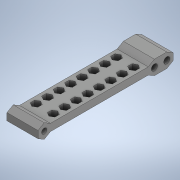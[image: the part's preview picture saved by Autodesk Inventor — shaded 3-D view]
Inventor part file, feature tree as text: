
AUTODESK INVENTOR PART (.ipt)
format: ipt  version: 2020 (Build 240168000, 168)  size: 455,680 bytes
history: native  units: in
note: dims shown in document units (in); Inventor stores cm internally (conversion verified against a paired STEP export)
features: sketch x7, extrude x6, projected_geometry x4, plane x2, mirror x1
ambient origin geometry x8: Origin, YZ Plane, XZ Plane, XY Plane, X Axis, Y Axis, Z Axis, Center Point
bodies: Solid1 (feature_tree)
feature tree (20):
  extrude  "Extrusion1"  Depth=3.4256in
  plane  "Work Plane1"
  extrude  "Extrusion2"  Depth=0.7874in
  sketch  "Sketch4"  dims[d4=0.0in d5=0.0827in]
  extrude  "Extrusion4"  Depth=0.0827in
  plane  "Work Plane2"
  extrude  "Extrusion6"  Depth=3.1106in
  mirror  "Mirror2"
  extrude  "Extrusion7"  Depth=0.315in
  extrude  "Extrusion8"  Depth=0.2362in
  sketch  "Sketch1"  dims[d0=0.1818in d1=3.4256in]
  sketch  "Sketch2"  dims[d2=0.1339in d3=0.7874in]
  sketch  "Sketch5"  dims[d6=0.7874in d7=0.0in d28=3.1106in]
  sketch  "Sketch7"  dims[d29=0.315in d31=0.315in]
  projected_geometry  "Projected Loop7"
  projected_geometry  "Projected Loop8"
  sketch  "Sketch8"  dims[d33=0.1575in d34=0.2362in]
  projected_geometry  "Projected Loop9"
  sketch  "Sketch10"  dims[d35=0.0in d38=0.315in d39=0.2756in d40=-0.3092in d41=0.0787in d42=0.0787in d43=0.0787in d44=3.1496in d46=0.2913in d47=0.3937in d49=0.3937in d51=3.1496in d53=0.2913in d54=0.3937in d56=0.3937in d58=0.0in d59=0.0in d60=150.0deg d61=0.1339in d62=0.1181in d63=1.9685in d64=0.1575in d65=0.0in]
  projected_geometry  "Projected Loop10"
